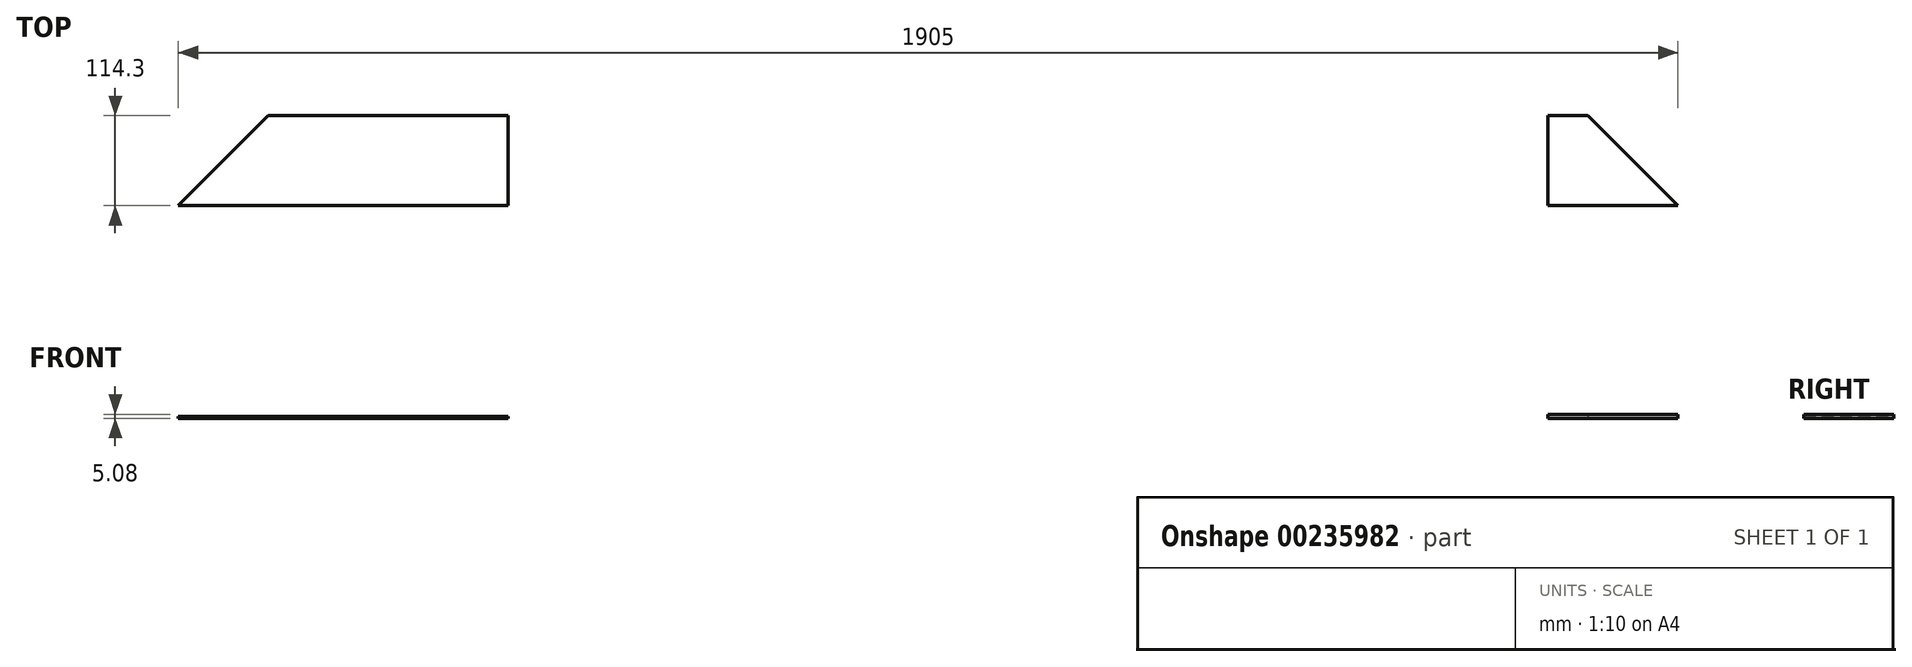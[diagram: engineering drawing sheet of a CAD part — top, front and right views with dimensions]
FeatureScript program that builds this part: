
annotation { "Feature Type Name" : "Feature", "Feature Type Description" : "" }
export const myFeature = defineFeature(function(context is Context, id is Id, definition is map)
    precondition{}
    {
        {
            var Q0;
            Q0=qCreatedBy(makeId("Top.planeOp"),FACE);
            var sketch = newSketch(context, id + "F0", { "sketchPlane" : qUnion([Q0])});
            skLineSegment(sketch, "E0.bottom", {"start": v(152.4, -57.15) * mm, "end": v(-152.4, -57.15) * mm});
            skLineSegment(sketch, "E0.top", {"start": v(152.4, 57.15) * mm, "end": v(-152.4, 57.15) * mm});
            skLineSegment(sketch, "E0.left", {"start": v(152.4, -57.15) * mm, "end": v(152.4, 57.15) * mm});
            skLineSegment(sketch, "E0.right", {"start": v(-152.4, -57.15) * mm, "end": v(-152.4, 57.15) * mm});
            skPoint(sketch, "E0.middle", {"position": v(0, 0) * mm});
            skLineSegment(sketch, "E1", {"start": v(-152.4, -57.15) * mm, "end": v(-266.7, -57.15) * mm});
            skLineSegment(sketch, "E2", {"start": v(-266.7, -57.15) * mm, "end": v(-152.4, 57.15) * mm});
            skLineSegment(sketch, "E3", {"start": v(-152.4, 57.15) * mm, "end": v(1524, 57.15) * mm});
            skLineSegment(sketch, "E4.bottom", {"start": v(1524, 57.15) * mm, "end": v(1473.2, 57.15) * mm});
            skLineSegment(sketch, "E4.top", {"start": v(1524, -57.15) * mm, "end": v(1473.2, -57.15) * mm});
            skLineSegment(sketch, "E4.left", {"start": v(1524, 57.15) * mm, "end": v(1524, -57.15) * mm});
            skLineSegment(sketch, "E4.right", {"start": v(1473.2, 57.15) * mm, "end": v(1473.2, -57.15) * mm});
            skLineSegment(sketch, "E5", {"start": v(1524, -57.15) * mm, "end": v(1638.3, -57.15) * mm});
            skLineSegment(sketch, "E6", {"start": v(1638.3, -57.15) * mm, "end": v(1524, 57.15) * mm});
            skSolve(sketch);
        }
        {
            var Q0;
            Q0 = qSketchRegion(id + "F0", true);
            extrude(context, id + "F1", {"entities" : qUnion([Q0]), "depth" : 2.54 * mm});
        }
        {
            var Q0;
            Q0=makeQuery(id+"F1.opExtrude","CAP_FACE",FACE,{"disambiguationData":[OSD([sQuery(id+"F0.wireOp",EDGE,"E4.bottom"),sQuery(id+"F0.wireOp",EDGE,"E4.top"),sQuery(id+"F0.wireOp",EDGE,"E4.right"),sQuery(id+"F0.wireOp",EDGE,"E5"),sQuery(id+"F0.wireOp",EDGE,"E6")])],"isStart":false});
            extrude(context, id + "F2", {"entities" : qUnion([Q0]), "operationType" : NewBodyOperationType.ADD, "depth" : 2.54 * mm});
        }
    });
